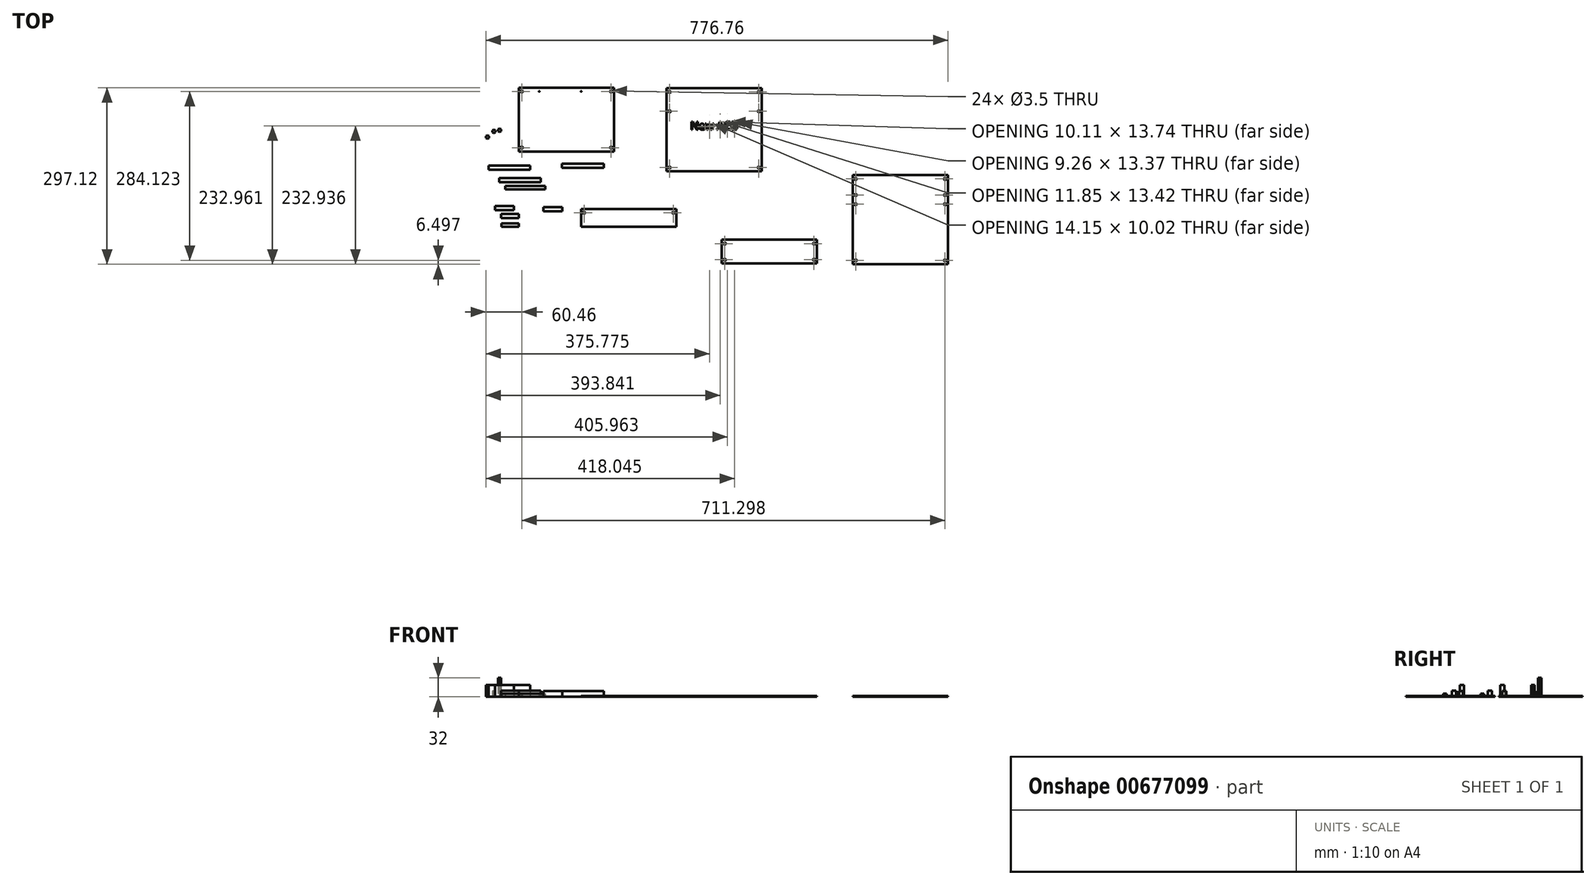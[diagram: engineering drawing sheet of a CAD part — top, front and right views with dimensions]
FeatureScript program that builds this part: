
annotation { "Feature Type Name" : "Feature", "Feature Type Description" : "" }
export const myFeature = defineFeature(function(context is Context, id is Id, definition is map)
    precondition{}
    {
        {
            var Q0;
            Q0=qCreatedBy(makeId("Top.planeOp"),FACE);
            var sketch = newSketch(context, id + "F0", { "sketchPlane" : qUnion([Q0])});
            skLineSegment(sketch, "E0.bottom", {"start": v(0, 0) * mm, "end": v(160, 0) * mm});
            skLineSegment(sketch, "E0.top", {"start": v(0, 107.5) * mm, "end": v(160, 107.5) * mm});
            skLineSegment(sketch, "E0.left", {"start": v(0, 0) * mm, "end": v(0, 107.5) * mm});
            skLineSegment(sketch, "E0.right", {"start": v(160, 0) * mm, "end": v(160, 107.5) * mm});
            skLineSegment(sketch, "E1", {"start": v(34.27, 115.15) * mm, "end": v(34.27, 89.45) * mm, "construction": true});
            skLineSegment(sketch, "E2", {"start": v(104.78, 115.15) * mm, "end": v(104.78, 86.57) * mm, "construction": true});
            skLineSegment(sketch, "E3.bottom", {"start": v(5, 101) * mm, "end": v(155, 101) * mm, "construction": true});
            skLineSegment(sketch, "E3.top", {"start": v(5, 6.5) * mm, "end": v(155, 6.5) * mm, "construction": true});
            skLineSegment(sketch, "E3.left", {"start": v(5, 101) * mm, "end": v(5, 6.5) * mm, "construction": true});
            skLineSegment(sketch, "E3.right", {"start": v(155, 101) * mm, "end": v(155, 6.5) * mm, "construction": true});
            skCircle(sketch, "E4", {"center": v(34.27, 101) * mm, "radius": 0.5 * mm});
            skCircle(sketch, "E5", {"center": v(104.78, 101) * mm, "radius": 0.5 * mm});
            skSolve(sketch);
        }
        {
            var Q0;
            Q0=makeQuery(id+"F0.imprint","IMPRINT",FACE,{"disambiguationData":[TD([[makeQuery(id+"F0.imprint","IMPRINT",EDGE,{"derivedFrom":sQuery(id+"F0.wireOp",EDGE,"E0.bottom")}),1.0]])]});
            extrude(context, id + "F1", {"entities" : qUnion([Q0]), "depth" : 1.6 * mm, "offsetDistance" : 25 * mm});
        }
        {
            var Q0;
            Q0=sQuery(id+"F0.wireOp",VERTEX,"E3.bottom.start");
            var Q1;
            Q1=sQuery(id+"F0.wireOp",VERTEX,"E3.bottom.end");
            var Q2;
            Q2=sQuery(id+"F0.wireOp",VERTEX,"E3.top.end");
            var Q3;
            Q3=sQuery(id+"F0.wireOp",VERTEX,"E3.top.start");
            var Q4;
            Q4=makeQuery(id+"F1.opExtrude","SWEPT_BODY",BODY,{"disambiguationData":[OSD([sQuery(id+"F0.wireOp",EDGE,"E0.bottom"),sQuery(id+"F0.wireOp",EDGE,"E0.top"),sQuery(id+"F0.wireOp",EDGE,"E0.left"),sQuery(id+"F0.wireOp",EDGE,"E0.right")])]});
            hole(context, id + "F2", {"style" : HoleStyle.SIMPLE, "endStyle" : HoleEndStyle.THROUGH, "oppositeDirection" : true, "holeDiameter" : 3.5 * mm, "majorDiameter" : 5 * mm, "isTappedThrough" : true, "tappedDepth" : 12 * mm, "tapClearance" : 3, "startFromSketch" : true, "locations" : qUnion([Q0, Q1, Q2, Q3]), "scope" : qUnion([Q4])});
        }
        {
            var Q0;
            Q0=qCreatedBy(makeId("Top.planeOp"),FACE);
            var sketch = newSketch(context, id + "F3", { "sketchPlane" : qUnion([Q0])});
            skLineSegment(sketch, "E6.bottom", {"start": v(-51.1, -23.64) * mm, "end": v(18.9, -23.64) * mm});
            skLineSegment(sketch, "E6.top", {"start": v(-51.1, -30.64) * mm, "end": v(18.9, -30.64) * mm});
            skLineSegment(sketch, "E6.left", {"start": v(-51.1, -23.64) * mm, "end": v(-51.1, -30.64) * mm});
            skLineSegment(sketch, "E6.right", {"start": v(18.9, -23.64) * mm, "end": v(18.9, -30.64) * mm});
            skSolve(sketch);
        }
        {
            var Q0;
            Q0=makeQuery(id+"F3.imprint","IMPRINT",FACE,{"disambiguationData":[TD([[makeQuery(id+"F3.imprint","IMPRINT",EDGE,{"derivedFrom":sQuery(id+"F3.wireOp",EDGE,"E6.bottom")}),-1.0]])]});
            extrude(context, id + "F4", {"entities" : qUnion([Q0]), "depth" : 20 * mm, "offsetDistance" : 25 * mm});
        }
        {
            var Q0;
            Q0=qCreatedBy(makeId("Top.planeOp"),FACE);
            var sketch = newSketch(context, id + "F5", { "sketchPlane" : qUnion([Q0])});
            skLineSegment(sketch, "E7.bottom", {"start": v(-33.26, -44.66) * mm, "end": v(36.74, -44.66) * mm});
            skLineSegment(sketch, "E7.top", {"start": v(-33.26, -51.66) * mm, "end": v(36.74, -51.66) * mm});
            skLineSegment(sketch, "E7.left", {"start": v(-33.26, -44.66) * mm, "end": v(-33.26, -51.66) * mm});
            skLineSegment(sketch, "E7.right", {"start": v(36.74, -44.66) * mm, "end": v(36.74, -51.66) * mm});
            skSolve(sketch);
        }
        {
            var Q0;
            Q0=makeQuery(id+"F5.imprint","IMPRINT",FACE,{"disambiguationData":[TD([[makeQuery(id+"F5.imprint","IMPRINT",EDGE,{"derivedFrom":sQuery(id+"F5.wireOp",EDGE,"E7.bottom")}),-1.0]])]});
            extrude(context, id + "F6", {"entities" : qUnion([Q0]), "depth" : 10.4 * mm, "offsetDistance" : 25 * mm});
        }
        {
            var Q0;
            Q0=qCreatedBy(makeId("Top.planeOp"),FACE);
            var sketch = newSketch(context, id + "F7", { "sketchPlane" : qUnion([Q0])});
            skLineSegment(sketch, "E8.bottom", {"start": v(-22.8, -58.18) * mm, "end": v(44.2, -58.18) * mm});
            skLineSegment(sketch, "E8.top", {"start": v(-22.8, -63.88) * mm, "end": v(44.2, -63.88) * mm});
            skLineSegment(sketch, "E8.left", {"start": v(-22.8, -58.18) * mm, "end": v(-22.8, -63.88) * mm});
            skLineSegment(sketch, "E8.right", {"start": v(44.2, -58.18) * mm, "end": v(44.2, -63.88) * mm});
            skSolve(sketch);
        }
        {
            var Q0;
            Q0=makeQuery(id+"F7.imprint","IMPRINT",FACE,{"disambiguationData":[TD([[makeQuery(id+"F7.imprint","IMPRINT",EDGE,{"derivedFrom":sQuery(id+"F7.wireOp",EDGE,"E8.bottom")}),-1.0]])]});
            extrude(context, id + "F8", {"entities" : qUnion([Q0]), "depth" : 5.5 * mm, "offsetDistance" : 25 * mm});
        }
        {
            var Q0;
            Q0=qCreatedBy(makeId("Top.planeOp"),FACE);
            var sketch = newSketch(context, id + "F9", { "sketchPlane" : qUnion([Q0])});
            skLineSegment(sketch, "E9.bottom", {"start": v(72.56, -20.42) * mm, "end": v(142.56, -20.42) * mm});
            skLineSegment(sketch, "E9.top", {"start": v(72.56, -27.42) * mm, "end": v(142.56, -27.42) * mm});
            skLineSegment(sketch, "E9.left", {"start": v(72.56, -20.42) * mm, "end": v(72.56, -27.42) * mm});
            skLineSegment(sketch, "E9.right", {"start": v(142.56, -20.42) * mm, "end": v(142.56, -27.42) * mm});
            skSolve(sketch);
        }
        {
            var Q0;
            Q0=makeQuery(id+"F9.imprint","IMPRINT",FACE,{"disambiguationData":[TD([[makeQuery(id+"F9.imprint","IMPRINT",EDGE,{"derivedFrom":sQuery(id+"F9.wireOp",EDGE,"E9.bottom")}),-1.0]])]});
            extrude(context, id + "F10", {"entities" : qUnion([Q0]), "depth" : 9.8 * mm, "offsetDistance" : 25 * mm});
        }
        {
            var Q0;
            Q0=qCreatedBy(makeId("Top.planeOp"),FACE);
            var sketch = newSketch(context, id + "F11", { "sketchPlane" : qUnion([Q0])});
            skLineSegment(sketch, "E10.bottom", {"start": v(-40, -91.42) * mm, "end": v(-8, -91.42) * mm});
            skLineSegment(sketch, "E10.top", {"start": v(-40, -98.42) * mm, "end": v(-8, -98.42) * mm});
            skLineSegment(sketch, "E10.left", {"start": v(-40, -91.42) * mm, "end": v(-40, -98.42) * mm});
            skLineSegment(sketch, "E10.right", {"start": v(-8, -91.42) * mm, "end": v(-8, -98.42) * mm});
            skSolve(sketch);
        }
        {
            var Q0;
            Q0=makeQuery(id+"F11.imprint","IMPRINT",FACE,{"disambiguationData":[TD([[makeQuery(id+"F11.imprint","IMPRINT",EDGE,{"derivedFrom":sQuery(id+"F11.wireOp",EDGE,"E10.bottom")}),-1.0]])]});
            extrude(context, id + "F12", {"entities" : qUnion([Q0]), "depth" : 20 * mm, "offsetDistance" : 25 * mm});
        }
        {
            var Q0;
            Q0=qCreatedBy(makeId("Top.planeOp"),FACE);
            var sketch = newSketch(context, id + "F13", { "sketchPlane" : qUnion([Q0])});
            skLineSegment(sketch, "E11.bottom", {"start": v(-30, -105.14) * mm, "end": v(0, -105.14) * mm});
            skLineSegment(sketch, "E11.top", {"start": v(-30, -112.14) * mm, "end": v(0, -112.14) * mm});
            skLineSegment(sketch, "E11.left", {"start": v(-30, -105.14) * mm, "end": v(-30, -112.14) * mm});
            skLineSegment(sketch, "E11.right", {"start": v(0, -105.14) * mm, "end": v(0, -112.14) * mm});
            skSolve(sketch);
        }
        {
            var Q0;
            Q0=makeQuery(id+"F13.imprint","IMPRINT",FACE,{"disambiguationData":[TD([[makeQuery(id+"F13.imprint","IMPRINT",EDGE,{"derivedFrom":sQuery(id+"F13.wireOp",EDGE,"E11.bottom")}),-1.0]])]});
            extrude(context, id + "F14", {"entities" : qUnion([Q0]), "depth" : 10.4 * mm, "offsetDistance" : 25 * mm});
        }
        {
            var Q0;
            Q0=qCreatedBy(makeId("Top.planeOp"),FACE);
            var sketch = newSketch(context, id + "F15", { "sketchPlane" : qUnion([Q0])});
            skLineSegment(sketch, "E12.bottom", {"start": v(-29, -120.64) * mm, "end": v(0, -120.64) * mm});
            skLineSegment(sketch, "E12.top", {"start": v(-29, -126.34) * mm, "end": v(0, -126.34) * mm});
            skLineSegment(sketch, "E12.left", {"start": v(-29, -120.64) * mm, "end": v(-29, -126.34) * mm});
            skLineSegment(sketch, "E12.right", {"start": v(0, -120.64) * mm, "end": v(0, -126.34) * mm});
            skSolve(sketch);
        }
        {
            var Q0;
            Q0=makeQuery(id+"F15.imprint","IMPRINT",FACE,{"disambiguationData":[TD([[makeQuery(id+"F15.imprint","IMPRINT",EDGE,{"derivedFrom":sQuery(id+"F15.wireOp",EDGE,"E12.bottom")}),-1.0]])]});
            extrude(context, id + "F16", {"entities" : qUnion([Q0]), "depth" : 5.5 * mm, "offsetDistance" : 25 * mm});
        }
        {
            var Q0;
            Q0=qCreatedBy(makeId("Top.planeOp"),FACE);
            var sketch = newSketch(context, id + "F17", { "sketchPlane" : qUnion([Q0])});
            skLineSegment(sketch, "E13.bottom", {"start": v(41.03, -93.71) * mm, "end": v(73.03, -93.71) * mm});
            skLineSegment(sketch, "E13.top", {"start": v(41.03, -100.71) * mm, "end": v(73.03, -100.71) * mm});
            skLineSegment(sketch, "E13.left", {"start": v(41.03, -93.71) * mm, "end": v(41.03, -100.71) * mm});
            skLineSegment(sketch, "E13.right", {"start": v(73.03, -93.71) * mm, "end": v(73.03, -100.71) * mm});
            skSolve(sketch);
        }
        {
            var Q0;
            Q0=makeQuery(id+"F17.imprint","IMPRINT",FACE,{"disambiguationData":[TD([[makeQuery(id+"F17.imprint","IMPRINT",EDGE,{"derivedFrom":sQuery(id+"F17.wireOp",EDGE,"E13.bottom")}),-1.0]])]});
            extrude(context, id + "F18", {"entities" : qUnion([Q0]), "depth" : 9.8 * mm, "offsetDistance" : 25 * mm});
        }
        {
            var Q0;
            Q0=qCreatedBy(makeId("Top.planeOp"),FACE);
            var sketch = newSketch(context, id + "F19", { "sketchPlane" : qUnion([Q0])});
            skCircle(sketch, "E14.cCircle", {"center": v(-52.9, 24.26) * mm, "radius": 2.5 * mm, "construction": true});
            skLineSegment(sketch, "E14.0", {"start": v(-52.82, 27.15) * mm, "end": v(-50.36, 25.63) * mm});
            skLineSegment(sketch, "E14.1", {"start": v(-50.36, 25.63) * mm, "end": v(-50.46, 22.74) * mm});
            skLineSegment(sketch, "E14.2", {"start": v(-50.46, 22.74) * mm, "end": v(-53, 21.38) * mm});
            skLineSegment(sketch, "E14.3", {"start": v(-53, 21.38) * mm, "end": v(-55.46, 22.9) * mm});
            skLineSegment(sketch, "E14.4", {"start": v(-55.46, 22.9) * mm, "end": v(-55.36, 25.79) * mm});
            skLineSegment(sketch, "E14.5", {"start": v(-55.36, 25.79) * mm, "end": v(-52.82, 27.15) * mm});
            skPoint(sketch, "E14.0.midPoint", {"position": v(-51.59, 26.39) * mm});
            skSolve(sketch);
        }
        {
            var Q0;
            Q0=makeQuery(id+"F19.imprint","IMPRINT",FACE,{"disambiguationData":[TD([[makeQuery(id+"F19.imprint","IMPRINT",EDGE,{"derivedFrom":sQuery(id+"F19.wireOp",EDGE,"E14.0")}),-1.0]])]});
            extrude(context, id + "F20", {"entities" : qUnion([Q0]), "depth" : 20 * mm, "offsetDistance" : 25 * mm});
        }
        {
            var Q0;
            Q0=qCreatedBy(makeId("Top.planeOp"),FACE);
            var sketch = newSketch(context, id + "F21", { "sketchPlane" : qUnion([Q0])});
            skLineSegment(sketch, "E15.bottom", {"start": v(104.6, -96.45) * mm, "end": v(264.6, -96.45) * mm});
            skLineSegment(sketch, "E15.top", {"start": v(104.6, -126.45) * mm, "end": v(264.6, -126.45) * mm});
            skLineSegment(sketch, "E15.left", {"start": v(104.6, -96.45) * mm, "end": v(104.6, -126.45) * mm});
            skLineSegment(sketch, "E15.right", {"start": v(264.6, -96.45) * mm, "end": v(264.6, -126.45) * mm});
            skCircle(sketch, "E16", {"center": v(109.6, -102.95) * mm, "radius": 1.75 * mm});
            skCircle(sketch, "E17", {"center": v(259.6, -102.95) * mm, "radius": 1.75 * mm});
            skSolve(sketch);
        }
        {
            var Q0;
            Q0=makeQuery(id+"F21.imprint","IMPRINT",FACE,{"disambiguationData":[TD([[makeQuery(id+"F21.imprint","IMPRINT",EDGE,{"derivedFrom":sQuery(id+"F21.wireOp",EDGE,"E15.bottom")}),-1.0]])]});
            extrude(context, id + "F22", {"entities" : qUnion([Q0]), "depth" : 1.6 * mm, "offsetDistance" : 25 * mm});
        }
        {
            var Q0;
            Q0=qCreatedBy(makeId("Top.planeOp"),FACE);
            var sketch = newSketch(context, id + "F23", { "sketchPlane" : qUnion([Q0])});
            skLineSegment(sketch, "E18.bottom", {"start": v(248.41, 106.6) * mm, "end": v(408.41, 106.6) * mm});
            skLineSegment(sketch, "E18.top", {"start": v(248.41, -33.4) * mm, "end": v(408.41, -33.4) * mm});
            skLineSegment(sketch, "E18.left", {"start": v(248.41, 106.6) * mm, "end": v(248.41, -33.4) * mm});
            skLineSegment(sketch, "E18.right", {"start": v(408.41, 106.6) * mm, "end": v(408.41, -33.4) * mm});
            skCircle(sketch, "E19", {"center": v(253.41, 100.1) * mm, "radius": 1.75 * mm});
            skCircle(sketch, "E20", {"center": v(403.41, 100.1) * mm, "radius": 1.75 * mm});
            skCircle(sketch, "E21", {"center": v(253.41, 67.6) * mm, "radius": 1.75 * mm});
            skCircle(sketch, "E22", {"center": v(403.41, 67.6) * mm, "radius": 1.75 * mm});
            skCircle(sketch, "E23", {"center": v(253.41, -26.9) * mm, "radius": 1.75 * mm});
            skCircle(sketch, "E24", {"center": v(403.41, -26.9) * mm, "radius": 1.75 * mm});
            skText(sketch, "E25", { "text": "New ACB", "fontName": "OpenSans-Regular.ttf"});
            const initialGuessF23  = {"E25": [0.28841, 0.03663, 1, 0, 0.01348]};
            skSetInitialGuess(sketch, initialGuessF23);
            skSolve(sketch);
        }
        {
            var Q0;
            Q0=makeQuery(id+"F23.imprint","IMPRINT",FACE,{"disambiguationData":[TD([[makeQuery(id+"F23.imprint","IMPRINT",EDGE,{"derivedFrom":sQuery(id+"F23.wireOp",EDGE,"E18.bottom")}),-1.0]])]});
            extrude(context, id + "F24", {"entities" : qUnion([Q0]), "depth" : 1.6 * mm, "offsetDistance" : 25 * mm});
        }
        {
            var Q0;
            Q0=qCreatedBy(makeId("Top.planeOp"),FACE);
            var sketch = newSketch(context, id + "F25", { "sketchPlane" : qUnion([Q0])});
            skCircle(sketch, "E26.cCircle", {"center": v(-41.73, 33.8) * mm, "radius": 2.5 * mm, "construction": true});
            skLineSegment(sketch, "E26.0", {"start": v(-39.25, 32.34) * mm, "end": v(-41.76, 30.91) * mm});
            skLineSegment(sketch, "E26.1", {"start": v(-41.76, 30.91) * mm, "end": v(-44.25, 32.38) * mm});
            skLineSegment(sketch, "E26.2", {"start": v(-44.25, 32.38) * mm, "end": v(-44.22, 35.26) * mm});
            skLineSegment(sketch, "E26.3", {"start": v(-44.22, 35.26) * mm, "end": v(-41.71, 36.69) * mm});
            skLineSegment(sketch, "E26.4", {"start": v(-41.71, 36.69) * mm, "end": v(-39.22, 35.22) * mm});
            skLineSegment(sketch, "E26.5", {"start": v(-39.22, 35.22) * mm, "end": v(-39.25, 32.34) * mm});
            skPoint(sketch, "E26.0.midPoint", {"position": v(-40.5, 31.63) * mm});
            skSolve(sketch);
        }
        {
            var Q0;
            Q0=makeQuery(id+"F25.imprint","IMPRINT",FACE,{"disambiguationData":[TD([[makeQuery(id+"F25.imprint","IMPRINT",EDGE,{"derivedFrom":sQuery(id+"F25.wireOp",EDGE,"E26.0")}),-1.0]])]});
            extrude(context, id + "F26", {"entities" : qUnion([Q0]), "depth" : 10 * mm, "offsetDistance" : 25 * mm});
        }
        {
            var Q0;
            Q0=qCreatedBy(makeId("Top.planeOp"),FACE);
            var sketch = newSketch(context, id + "F27", { "sketchPlane" : qUnion([Q0])});
            skCircle(sketch, "E27.cCircle", {"center": v(-32.14, 35.9) * mm, "radius": 2.5 * mm, "construction": true});
            skLineSegment(sketch, "E27.0", {"start": v(-29.63, 34.48) * mm, "end": v(-32.12, 33.02) * mm});
            skLineSegment(sketch, "E27.1", {"start": v(-32.12, 33.02) * mm, "end": v(-34.63, 34.45) * mm});
            skLineSegment(sketch, "E27.2", {"start": v(-34.63, 34.45) * mm, "end": v(-34.65, 37.33) * mm});
            skLineSegment(sketch, "E27.3", {"start": v(-34.65, 37.33) * mm, "end": v(-32.15, 38.8) * mm});
            skLineSegment(sketch, "E27.4", {"start": v(-32.15, 38.8) * mm, "end": v(-29.65, 37.36) * mm});
            skLineSegment(sketch, "E27.5", {"start": v(-29.65, 37.36) * mm, "end": v(-29.63, 34.48) * mm});
            skPoint(sketch, "E27.0.midPoint", {"position": v(-30.88, 33.75) * mm});
            skSolve(sketch);
        }
        {
            var Q0;
            Q0=makeQuery(id+"F27.imprint","IMPRINT",FACE,{"disambiguationData":[TD([[makeQuery(id+"F27.imprint","IMPRINT",EDGE,{"derivedFrom":sQuery(id+"F27.wireOp",EDGE,"E27.0")}),-1.0]])]});
            extrude(context, id + "F28", {"entities" : qUnion([Q0]), "depth" : 32 * mm, "offsetDistance" : 25 * mm});
        }
        {
            var Q0;
            Q0=qCreatedBy(makeId("Top.planeOp"),FACE);
            var sketch = newSketch(context, id + "F29", { "sketchPlane" : qUnion([Q0])});
            skLineSegment(sketch, "E28.bottom", {"start": v(341.16, -148.37) * mm, "end": v(501.16, -148.37) * mm});
            skLineSegment(sketch, "E28.top", {"start": v(341.16, -188.37) * mm, "end": v(501.16, -188.37) * mm});
            skLineSegment(sketch, "E28.left", {"start": v(341.16, -148.37) * mm, "end": v(341.16, -188.37) * mm});
            skLineSegment(sketch, "E28.right", {"start": v(501.16, -148.37) * mm, "end": v(501.16, -188.37) * mm});
            skCircle(sketch, "E29", {"center": v(346.16, -154.87) * mm, "radius": 1.75 * mm});
            skCircle(sketch, "E30", {"center": v(346.16, -181.87) * mm, "radius": 1.75 * mm});
            skCircle(sketch, "E31", {"center": v(496.16, -154.87) * mm, "radius": 1.75 * mm});
            skCircle(sketch, "E32", {"center": v(496.16, -181.87) * mm, "radius": 1.75 * mm});
            skSolve(sketch);
        }
        {
            var Q0;
            Q0=qCreatedBy(makeId("Top.planeOp"),FACE);
            var sketch = newSketch(context, id + "F30", { "sketchPlane" : qUnion([Q0])});
            skLineSegment(sketch, "E33.bottom", {"start": v(561.3, -39.62) * mm, "end": v(721.3, -39.62) * mm});
            skLineSegment(sketch, "E33.top", {"start": v(561.3, -189.62) * mm, "end": v(721.3, -189.62) * mm});
            skLineSegment(sketch, "E33.left", {"start": v(561.3, -39.62) * mm, "end": v(561.3, -189.62) * mm});
            skLineSegment(sketch, "E33.right", {"start": v(721.3, -39.62) * mm, "end": v(721.3, -189.62) * mm});
            skCircle(sketch, "E34", {"center": v(566.3, -183.12) * mm, "radius": 1.75 * mm});
            skCircle(sketch, "E35", {"center": v(716.3, -183.12) * mm, "radius": 1.75 * mm});
            skCircle(sketch, "E36", {"center": v(566.3, -88.62) * mm, "radius": 1.75 * mm});
            skCircle(sketch, "E37", {"center": v(716.3, -88.62) * mm, "radius": 1.75 * mm});
            skCircle(sketch, "E38", {"center": v(566.3, -73.12) * mm, "radius": 1.75 * mm});
            skCircle(sketch, "E39", {"center": v(716.3, -73.12) * mm, "radius": 1.75 * mm});
            skCircle(sketch, "E40", {"center": v(716.3, -46.12) * mm, "radius": 1.75 * mm});
            skCircle(sketch, "E41", {"center": v(566.3, -46.12) * mm, "radius": 1.75 * mm});
            skSolve(sketch);
        }
        {
            var Q0;
            Q0=makeQuery(id+"F29.imprint","IMPRINT",FACE,{"disambiguationData":[TD([[makeQuery(id+"F29.imprint","IMPRINT",EDGE,{"derivedFrom":sQuery(id+"F29.wireOp",EDGE,"E28.bottom")}),-1.0]])]});
            extrude(context, id + "F31", {"entities" : qUnion([Q0]), "depth" : 1.6 * mm, "offsetDistance" : 25 * mm});
        }
        {
            var Q0;
            Q0=makeQuery(id+"F30.imprint","IMPRINT",FACE,{"disambiguationData":[TD([[makeQuery(id+"F30.imprint","IMPRINT",EDGE,{"derivedFrom":sQuery(id+"F30.wireOp",EDGE,"E33.bottom")}),-1.0]])]});
            extrude(context, id + "F32", {"entities" : qUnion([Q0]), "depth" : 1.6 * mm, "offsetDistance" : 25 * mm});
        }
    });
